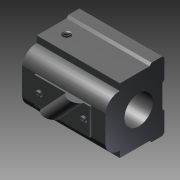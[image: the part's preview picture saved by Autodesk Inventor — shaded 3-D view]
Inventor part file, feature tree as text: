
AUTODESK INVENTOR PART (.ipt)
format: ipt  version: 2011 SP1 (Build 150282100, 282)  size: 206,336 bytes
history: native  units: mm
features: sketch x9, other x7, extrude x5, revolve x2, hole x2, pattern_linear x1
ambient origin geometry x8: Origin, YZ Plane, XZ Plane, XY Plane, X Axis, Y Axis, Z Axis, Center Point
bodies: Solid1 (feature_tree)
feature tree (26):
  extrude  "Extrusion1"  Depth=58.0mm TaperAngle=0.0deg
  extrude  "Extrusion2"  TaperAngle=360.0deg  [1 undecoded]
  extrude  "Extrusion3"  Depth=0.8mm TaperAngle=0.0deg
  revolve  "Revolution1"  [1 undecoded]
  revolve  "Revolution2"  [1 undecoded]
  extrude  "Extrusion4"  [1 undecoded]
  extrude  "Extrusion5"  [1 undecoded]
  hole  "Hole1"  [1 undecoded]
  hole  "Hole2"  [1 undecoded]
  pattern_linear  "Rectangular Pattern1"  [2 undecoded]
  other  "bnt_nut_1_XY"
  other  "bnt_nut_1_YZ"
  other  "bnt_nut_1_ZX"
  other  "bnt_nut_1_X"
  other  "bnt_nut_1_Y"
  other  "bnt_nut_1_Z"
  other  "bnt_nut_1_Center"
  sketch  "Sketch_1"  dims[d0=58.0mm d1=0.0mm d2=58.0mm d3=0.0mm]
  sketch  "Sketch_2"  dims[d4=4.6mm d5=0.0mm d6=360.0deg]
  sketch  "Sketch_3"  dims[d7=360.0deg d8=0.8mm d9=0.0mm]
  sketch  "Sketch_4"  dims[d10=0.8mm d11=0.0mm]
  sketch  "Sketch_5"  dims[d12=4.917mm d13=10.5415mm d14=6.0mm d15=2.0mm d16=90.0deg d17=14.140584mm d18=120.0deg]
  sketch  "Sketch_6"  dims[d19=4.917mm d20=10.5415mm d21=6.0mm d22=2.0mm d23=90.0deg d24=13.140584mm d25=120.0deg d26=20.0mm d28=35.0mm d29=20.0mm d31=35.0mm]
  sketch  "Sketch_7"  dims[d32=0.0mm]
  sketch  "Sketch8"
  sketch  "Sketch9"
note: 9 required parameter values undecoded (feature->parameter linkage not recoverable at this tier; creation-order binding heuristic only, values carry confidence <= 0.55)